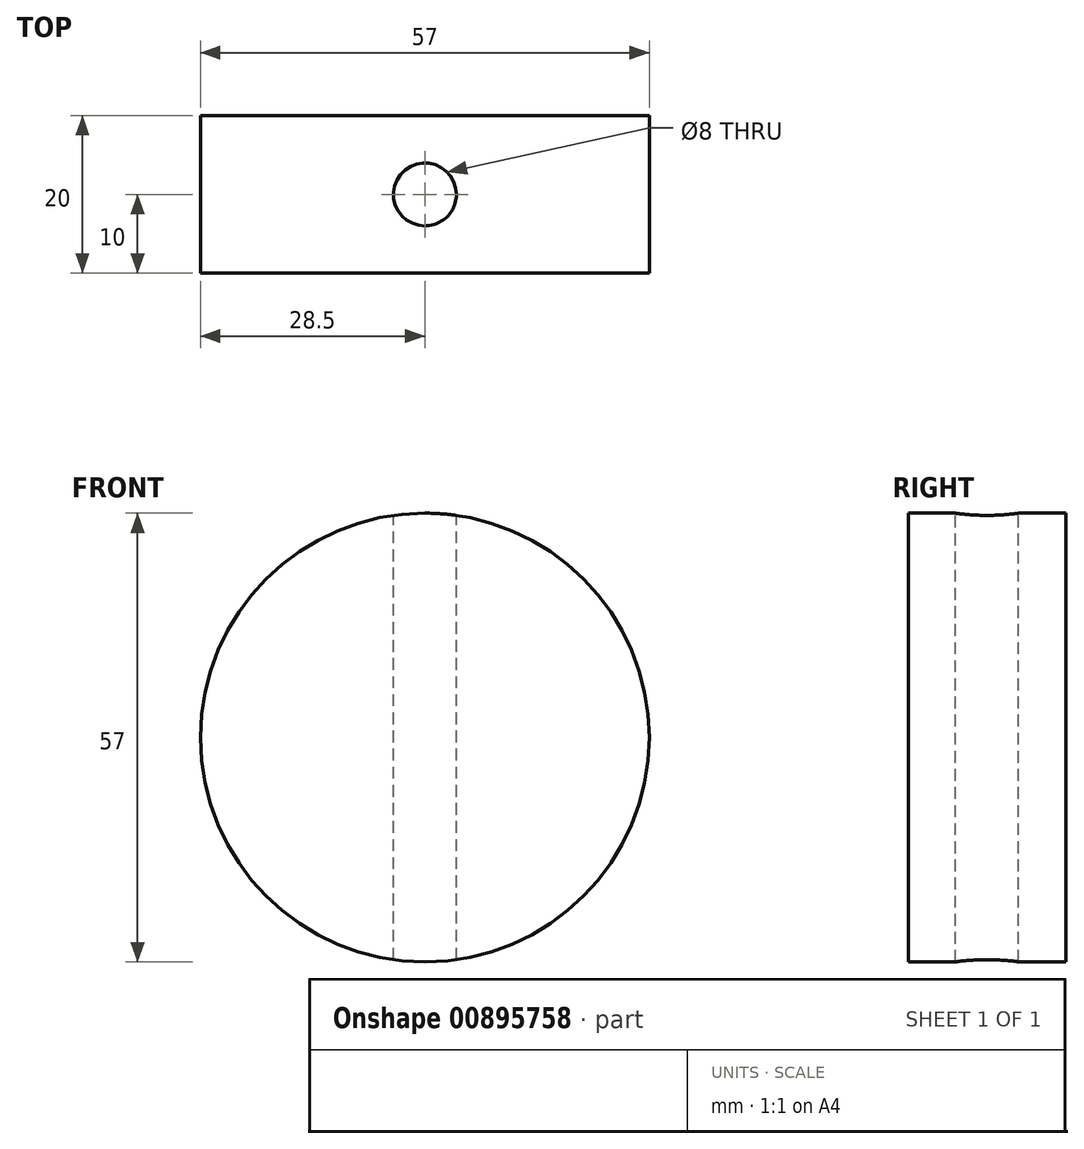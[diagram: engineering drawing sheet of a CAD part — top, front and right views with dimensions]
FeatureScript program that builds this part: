
annotation { "Feature Type Name" : "Feature", "Feature Type Description" : "" }
export const myFeature = defineFeature(function(context is Context, id is Id, definition is map)
    precondition{}
    {
        {
            var Q0;
            Q0=qCreatedBy(makeId("Front.planeOp"),FACE);
            var sketch = newSketch(context, id + "F0", { "sketchPlane" : qUnion([Q0])});
            skCircle(sketch, "E0", {"center": v(0, 0) * mm, "radius": 28.5 * mm});
            skPoint(sketch, "E1", {"position": v(-28.5, 0) * mm});
            skSolve(sketch);
        }
        {
            var Q0;
            Q0=makeQuery(id+"F0.imprint","IMPRINT",FACE,{"disambiguationData":[TD([[makeQuery(id+"F0.imprint","IMPRINT",EDGE,{"derivedFrom":sQuery(id+"F0.wireOp",EDGE,"E0")}),1.0]])]});
            extrude(context, id + "F1", {"entities" : qUnion([Q0]), "offsetDistance" : 25 * mm, "depth" : 20 * mm});
        }
        {
            var Q0;
            Q0=qCreatedBy(makeId("Top.planeOp"),FACE);
            var sketch = newSketch(context, id + "F2", { "sketchPlane" : qUnion([Q0])});
            skCircle(sketch, "E2", {"center": v(0, -10) * mm, "radius": 4 * mm});
            skSolve(sketch);
        }
        {
            var Q0;
            Q0=qSketchRegion(id+"F2",true);
            extrude(context, id + "F3", {"entities" : qUnion([Q0]), "operationType" : NewBodyOperationType.REMOVE, "endBound" : BoundingType.THROUGH_ALL, "oppositeDirection" : true, "depth" : 50 * mm});
        }
        {
            var Q0;
            Q0=qSketchRegion(id+"F2",true);
            extrude(context, id + "F4", {"entities" : qUnion([Q0]), "operationType" : NewBodyOperationType.REMOVE, "endBound" : BoundingType.THROUGH_ALL, "depth" : 25 * mm});
        }
    });
